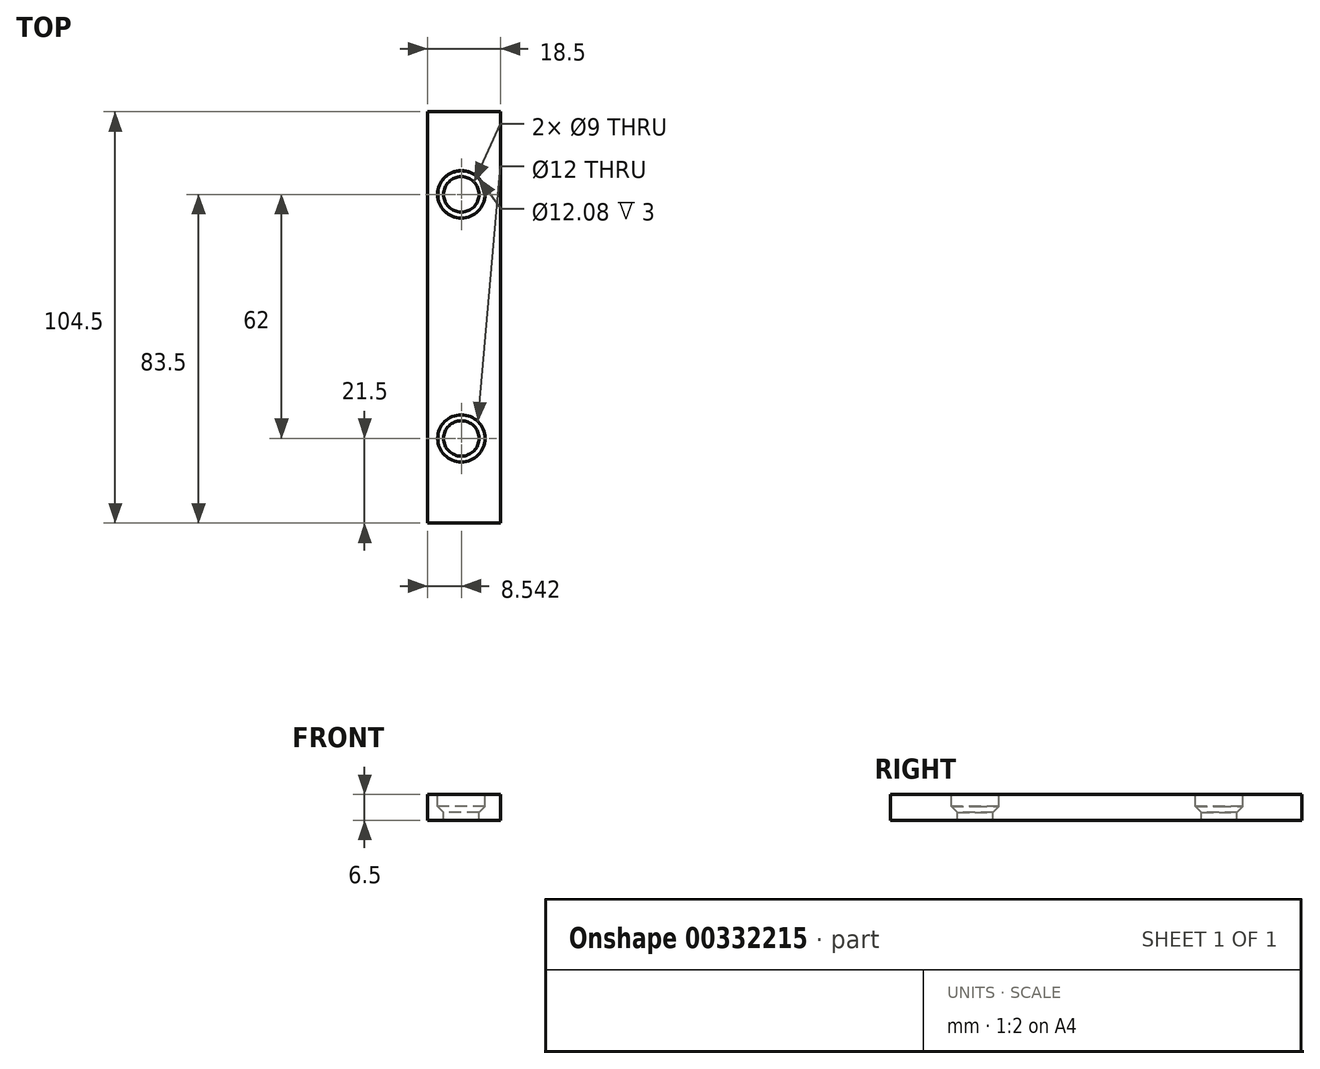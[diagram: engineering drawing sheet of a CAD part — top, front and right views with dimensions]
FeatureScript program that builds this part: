
annotation { "Feature Type Name" : "Feature", "Feature Type Description" : "" }
export const myFeature = defineFeature(function(context is Context, id is Id, definition is map)
    precondition{}
    {
        {
            var Q0;
            Q0=qCreatedBy(makeId("Top.planeOp"),FACE);
            var sketch = newSketch(context, id + "F0", { "sketchPlane" : qUnion([Q0])});
            skLineSegment(sketch, "E0.bottom", {"start": v(-9.25, 52.25) * mm, "end": v(9.25, 52.25) * mm});
            skLineSegment(sketch, "E0.top", {"start": v(-9.25, -52.25) * mm, "end": v(9.25, -52.25) * mm});
            skLineSegment(sketch, "E0.left", {"start": v(-9.25, 52.25) * mm, "end": v(-9.25, -52.25) * mm});
            skLineSegment(sketch, "E0.right", {"start": v(9.25, 52.25) * mm, "end": v(9.25, -52.25) * mm});
            skPoint(sketch, "E0.middle", {"position": v(0, 0) * mm});
            skSolve(sketch);
        }
        {
            var Q0;
            Q0 = qSketchRegion(id + "F0", true);
            extrude(context, id + "F1", {"entities" : qUnion([Q0]), "depth" : 6.5 * mm});
        }
        {
            var Q0;
            Q0=makeQuery(id+"F1.opExtrude","CAP_FACE",FACE,{"disambiguationData":[OSD([sQuery(id+"F0.wireOp",EDGE,"E0.bottom"),sQuery(id+"F0.wireOp",EDGE,"E0.top"),sQuery(id+"F0.wireOp",EDGE,"E0.left"),sQuery(id+"F0.wireOp",EDGE,"E0.right")])],"isStart":false});
            var sketch = newSketch(context, id + "F2", { "sketchPlane" : qUnion([Q0])});
            skLineSegment(sketch, "E1", {"start": v(0, 52.25) * mm, "end": v(0, 25.25) * mm});
            skPoint(sketch, "E2", {"position": v(0, 37.25) * mm});
            skPoint(sketch, "E3", {"position": v(0, 31.25) * mm});
            skLineSegment(sketch, "E4", {"start": v(-9.25, 31.25) * mm, "end": v(9.25, 31.25) * mm});
            skPoint(sketch, "E5", {"position": v(-6.75, 31.25) * mm});
            skCircle(sketch, "E6", {"center": v(-0.7, 31.25) * mm, "radius": 6.04 * mm});
            skLineSegment(sketch, "E7", {"start": v(-0.7, 31.25) * mm, "end": v(-0.7, -52.25) * mm});
            skPoint(sketch, "E8", {"position": v(-0.7, -24.75) * mm});
            skPoint(sketch, "E9", {"position": v(-0.7, -52.25) * mm});
            skPoint(sketch, "E10", {"position": v(-0.7, -38.5) * mm});
            skPoint(sketch, "E11", {"position": v(-0.7, -36.75) * mm});
            skPoint(sketch, "E12", {"position": v(-0.7, -30.75) * mm});
            skCircle(sketch, "E13", {"center": v(-0.7, -30.75) * mm, "radius": 6 * mm});
            skSolve(sketch);
        }
        {
            var Q0;
            {var subQ0=sQuery(id+"F2.wireOp",EDGE,"E6");var subQ1=sQuery(id+"F2.wireOp",EDGE,"E1");var subQ2=makeQuery(id+"F2.imprint","INTERSECT",VERTEX,{"disambiguationData":[OD(1.0)],"derivedFrom":[subQ1,subQ0]});Q0=makeQuery(id+"F2.imprint","IMPRINT",FACE,{"disambiguationData":[TD([[makeQuery(id+"F2.imprint","IMPRINT",EDGE,{"disambiguationData":[TD([[subQ2,-1.0]])],"derivedFrom":subQ1}),-1.0]])]});}
            var Q1;
            {var subQ0=sQuery(id+"F2.wireOp",EDGE,"E6");var subQ1=sQuery(id+"F2.wireOp",EDGE,"E1");var subQ2=makeQuery(id+"F2.imprint","INTERSECT",VERTEX,{"disambiguationData":[OD(1.0)],"derivedFrom":[subQ1,subQ0]});Q1=makeQuery(id+"F2.imprint","IMPRINT",FACE,{"disambiguationData":[TD([[makeQuery(id+"F2.imprint","IMPRINT",EDGE,{"disambiguationData":[TD([[subQ2,-1.0]])],"derivedFrom":subQ1}),1.0]])]});}
            var Q2;
            {var subQ0=sQuery(id+"F2.wireOp",EDGE,"E6");var subQ1=sQuery(id+"F2.wireOp",EDGE,"E1");var subQ2=makeQuery(id+"F2.imprint","INTERSECT",VERTEX,{"disambiguationData":[OD(0.0)],"derivedFrom":[subQ1,subQ0]});Q2=makeQuery(id+"F2.imprint","IMPRINT",FACE,{"disambiguationData":[TD([[makeQuery(id+"F2.imprint","IMPRINT",EDGE,{"disambiguationData":[TD([[subQ2,1.0]])],"derivedFrom":subQ1}),1.0]])]});}
            var Q3;
            {var subQ0=sQuery(id+"F2.wireOp",EDGE,"E6");var subQ1=sQuery(id+"F2.wireOp",EDGE,"E1");var subQ2=makeQuery(id+"F2.imprint","INTERSECT",VERTEX,{"disambiguationData":[OD(0.0)],"derivedFrom":[subQ1,subQ0]});Q3=makeQuery(id+"F2.imprint","IMPRINT",FACE,{"disambiguationData":[TD([[makeQuery(id+"F2.imprint","IMPRINT",EDGE,{"disambiguationData":[TD([[subQ2,1.0]])],"derivedFrom":subQ1}),-1.0]])]});}
            var Q4;
            {var subQ0=sQuery(id+"F2.wireOp",EDGE,"E7");var subQ1=sQuery(id+"F2.wireOp",EDGE,"E4");var subQ2=makeQuery(id+"F2.imprint","INTERSECT",VERTEX,{"derivedFrom":[subQ1,subQ0]});Q4=makeQuery(id+"F2.imprint","IMPRINT",FACE,{"disambiguationData":[TD([[makeQuery(id+"F2.imprint","IMPRINT",EDGE,{"disambiguationData":[TD([[subQ2,1.0]])],"derivedFrom":subQ1}),-1.0]])]});}
            var Q5;
            {var subQ0=sQuery(id+"F2.wireOp",EDGE,"E13");var subQ1=sQuery(id+"F2.wireOp",EDGE,"E7");var subQ2=makeQuery(id+"F2.imprint","INTERSECT",VERTEX,{"disambiguationData":[OD(0.0)],"derivedFrom":[subQ1,subQ0]});Q5=makeQuery(id+"F2.imprint","IMPRINT",FACE,{"disambiguationData":[TD([[makeQuery(id+"F2.imprint","IMPRINT",EDGE,{"disambiguationData":[TD([[subQ2,-1.0]])],"derivedFrom":subQ1}),1.0]])]});}
            var Q6;
            {var subQ0=sQuery(id+"F2.wireOp",EDGE,"E13");var subQ1=sQuery(id+"F2.wireOp",EDGE,"E7");var subQ2=makeQuery(id+"F2.imprint","INTERSECT",VERTEX,{"disambiguationData":[OD(0.0)],"derivedFrom":[subQ1,subQ0]});Q6=makeQuery(id+"F2.imprint","IMPRINT",FACE,{"disambiguationData":[TD([[makeQuery(id+"F2.imprint","IMPRINT",EDGE,{"disambiguationData":[TD([[subQ2,-1.0]])],"derivedFrom":subQ1}),-1.0]])]});}
            extrude(context, id + "F3", {"entities" : qUnion([Q0, Q1, Q2, Q3, Q4, Q5, Q6]), "operationType" : NewBodyOperationType.REMOVE, "oppositeDirection" : true, "depth" : 3 * mm});
        }
        {
            var Q0;
            Q0=makeQuery(id+"F3.boolean.opBoolean","COPY",FACE,{"derivedFrom":makeQuery(id+"F3.opExtrude","CAP_FACE",FACE,{"disambiguationData":[OSD([sQuery(id+"F2.wireOp",EDGE,"E6")])],"isStart":false})});
            var sketch = newSketch(context, id + "F4", { "sketchPlane" : qUnion([Q0])});
            skCircle(sketch, "E14", {"center": v(-0.7, 31.25) * mm, "radius": 6 * mm});
            skSolve(sketch);
        }
        {
            var Q0;
            Q0=sQuery(id+"F4.wireOp",VERTEX,"E14.center");
            var Q1;
            Q1=makeQuery(id+"F1.opExtrude","SWEPT_BODY",BODY,{"disambiguationData":[OSD([sQuery(id+"F0.wireOp",EDGE,"E0.bottom"),sQuery(id+"F0.wireOp",EDGE,"E0.top"),sQuery(id+"F0.wireOp",EDGE,"E0.left"),sQuery(id+"F0.wireOp",EDGE,"E0.right")])]});
            hole(context, id + "F5", {"style" : HoleStyle.C_SINK, "endStyle" : HoleEndStyle.THROUGH, "holeDiameter" : 9 * mm, "cSinkDiameter" : 12 * mm, "cSinkAngle" : 90 * degree, "tappedDepth" : 12 * mm, "tapClearance" : 3, "startFromSketch" : true, "locations" : qUnion([Q0]), "scope" : qUnion([Q1])});
        }
        {
            var Q0;
            Q0=makeQuery(id+"F3.boolean.opBoolean","COPY",FACE,{"derivedFrom":makeQuery(id+"F3.opExtrude","CAP_FACE",FACE,{"disambiguationData":[OSD([sQuery(id+"F2.wireOp",EDGE,"E13")])],"isStart":false})});
            var sketch = newSketch(context, id + "F6", { "sketchPlane" : qUnion([Q0])});
            skCircle(sketch, "E15", {"center": v(-0.7, -30.75) * mm, "radius": 6 * mm});
            skSolve(sketch);
        }
        {
            var Q0;
            Q0=sQuery(id+"F6.wireOp",VERTEX,"E15.center");
            var Q1;
            Q1=makeQuery(id+"F1.opExtrude","SWEPT_BODY",BODY,{"disambiguationData":[OSD([sQuery(id+"F0.wireOp",EDGE,"E0.bottom"),sQuery(id+"F0.wireOp",EDGE,"E0.top"),sQuery(id+"F0.wireOp",EDGE,"E0.left"),sQuery(id+"F0.wireOp",EDGE,"E0.right")])]});
            hole(context, id + "F7", {"style" : HoleStyle.C_SINK, "endStyle" : HoleEndStyle.THROUGH, "holeDiameter" : 9 * mm, "cSinkDiameter" : 12 * mm, "cSinkAngle" : 90 * degree, "tappedDepth" : 12 * mm, "tapClearance" : 3, "startFromSketch" : true, "locations" : qUnion([Q0]), "scope" : qUnion([Q1])});
        }
    });
